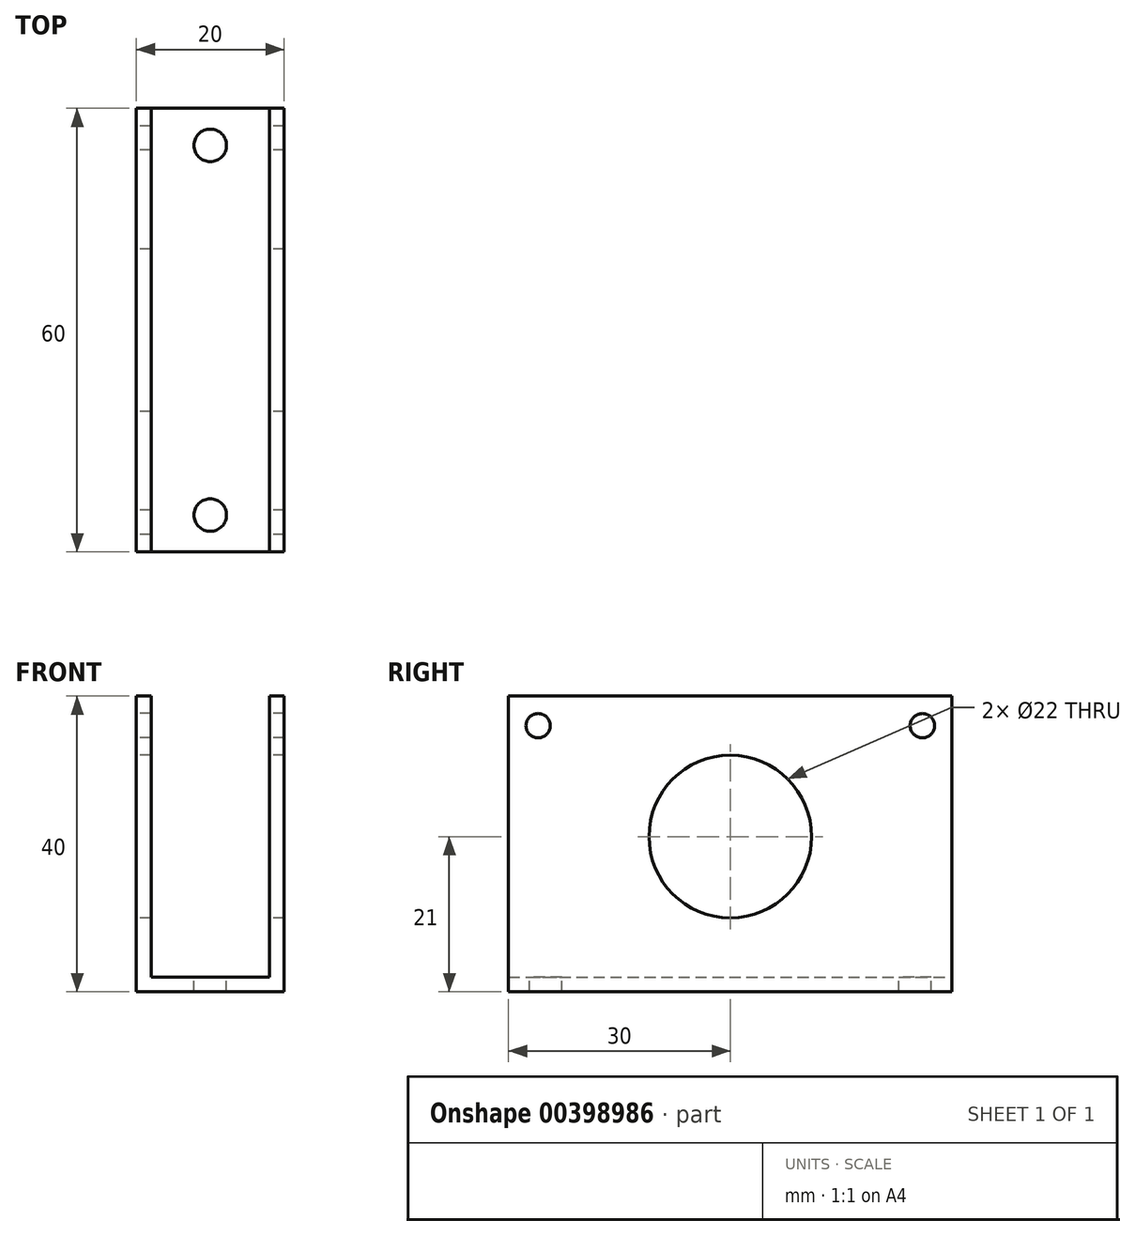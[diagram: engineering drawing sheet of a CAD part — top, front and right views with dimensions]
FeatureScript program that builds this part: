
annotation { "Feature Type Name" : "Feature", "Feature Type Description" : "" }
export const myFeature = defineFeature(function(context is Context, id is Id, definition is map)
    precondition{}
    {
        {
            var Q0;
            Q0=qCreatedBy(makeId("Front.planeOp"),FACE);
            var sketch = newSketch(context, id + "F0", { "sketchPlane" : qUnion([Q0])});
            skLineSegment(sketch, "E0", {"start": v(-10, 40) * mm, "end": v(-8, 40) * mm});
            skLineSegment(sketch, "E1", {"start": v(-8, 40) * mm, "end": v(-8, 2) * mm});
            skLineSegment(sketch, "E2", {"start": v(-8, 2) * mm, "end": v(0, 2) * mm});
            skLineSegment(sketch, "E3", {"start": v(-10, 40) * mm, "end": v(-10, 0) * mm});
            skLineSegment(sketch, "E4", {"start": v(-10, 0) * mm, "end": v(0, 0) * mm});
            skLineSegment(sketch, "E5.MirrorCS", {"start": v(8, 40) * mm, "end": v(8, 2) * mm});
            skLineSegment(sketch, "E6.MirrorCS", {"start": v(10, 40) * mm, "end": v(10, 0) * mm});
            skLineSegment(sketch, "E7.MirrorCS", {"start": v(10, 40) * mm, "end": v(8, 40) * mm});
            skLineSegment(sketch, "E8.MirrorCS", {"start": v(8, 2) * mm, "end": v(0, 2) * mm});
            skLineSegment(sketch, "E9.MirrorCS", {"start": v(10, 0) * mm, "end": v(0, 0) * mm});
            skSolve(sketch);
        }
        {
            var Q0;
            Q0=makeQuery(id+"F0.imprint","IMPRINT",FACE,{"disambiguationData":[TD([[makeQuery(id+"F0.imprint","IMPRINT",EDGE,{"derivedFrom":sQuery(id+"F0.wireOp",EDGE,"E0")}),-1.0]])]});
            extrude(context, id + "F1", {"entities" : qUnion([Q0]), "depth" : 60 * mm, "symmetric" : true});
        }
        {
            var Q0;
            Q0=makeQuery(id+"F1.opExtrude","SWEPT_FACE",FACE,{"disambiguationData":[OSD([sQuery(id+"F0.wireOp",EDGE,"E3")])]});
            var sketch = newSketch(context, id + "F2", { "sketchPlane" : qUnion([Q0])});
            skCircle(sketch, "E10", {"center": v(0, 21) * mm, "radius": 11 * mm});
            skPoint(sketch, "E11", {"position": v(-26, 36) * mm});
            skPoint(sketch, "E12.MirrorP", {"position": v(26, 36) * mm});
            skSolve(sketch);
        }
        {
            var Q0;
            Q0=makeQuery(id+"F2.imprint","IMPRINT",FACE,{"disambiguationData":[TD([[makeQuery(id+"F2.imprint","IMPRINT",EDGE,{"derivedFrom":sQuery(id+"F2.wireOp",EDGE,"E10")}),1.0]])]});
            var Q1;
            Q1=makeQuery(id+"F1.opExtrude","SWEPT_FACE",FACE,{"disambiguationData":[OSD([sQuery(id+"F0.wireOp",EDGE,"E6.MirrorCS")])]});
            extrude(context, id + "F3", {"entities" : qUnion([Q0]), "operationType" : NewBodyOperationType.REMOVE, "endBound" : BoundingType.UP_TO_SURFACE, "oppositeDirection" : true, "endBoundEntityFace" : qUnion([Q1]), "depth" : 25 * mm});
        }
        {
            var Q0;
            Q0=makeQuery(id+"F1.opExtrude","SWEPT_FACE",FACE,{"disambiguationData":[OSD([sQuery(id+"F0.wireOp",EDGE,"E2"),sQuery(id+"F0.wireOp",EDGE,"E8.MirrorCS")])]});
            var sketch = newSketch(context, id + "F4", { "sketchPlane" : qUnion([Q0])});
            skLineSegment(sketch, "E13", {"start": v(0, 30) * mm, "end": v(0, -30) * mm, "construction": true});
            skPoint(sketch, "E14", {"position": v(0, 25) * mm});
            skLineSegment(sketch, "E15", {"start": v(8, 0) * mm, "end": v(-8, 0) * mm, "construction": true});
            skPoint(sketch, "E16.MirrorP", {"position": v(0, -25) * mm});
            skSolve(sketch);
        }
        {
            var Q0;
            Q0=sQuery(id+"F4.wireOp",VERTEX,"E14");
            var Q1;
            Q1=sQuery(id+"F4.wireOp",VERTEX,"E16.MirrorP");
            var Q2;
            Q2=makeQuery(id+"F1.opExtrude","SWEPT_BODY",BODY,{"disambiguationData":[OSD([sQuery(id+"F0.wireOp",EDGE,"E0"),sQuery(id+"F0.wireOp",EDGE,"E1"),sQuery(id+"F0.wireOp",EDGE,"E2"),sQuery(id+"F0.wireOp",EDGE,"E3"),sQuery(id+"F0.wireOp",EDGE,"E4"),sQuery(id+"F0.wireOp",EDGE,"E5.MirrorCS"),sQuery(id+"F0.wireOp",EDGE,"E6.MirrorCS"),sQuery(id+"F0.wireOp",EDGE,"E7.MirrorCS"),sQuery(id+"F0.wireOp",EDGE,"E8.MirrorCS"),sQuery(id+"F0.wireOp",EDGE,"E9.MirrorCS")])]});
            hole(context, id + "F5", {"style" : HoleStyle.SIMPLE, "endStyle" : HoleEndStyle.THROUGH, "standardTappedOrClearance" : lookupTablePath({ "standard" : "ISO", "fit" : "Normal", "size" : "M4", "type" : "Clearance" }), "standardBlindInLast" : lookupTablePath({ "fit" : "Standard", "standard" : "ISO", "size" : "M4", "type" : "Clearance" }), "holeDiameter" : 4.4 * mm, "isTappedThrough" : true, "tappedDepth" : 3 * mm, "tapClearance" : 3, "locations" : qUnion([Q0, Q1]), "scope" : qUnion([Q2])});
        }
        {
            var Q0;
            Q0=sQuery(id+"F2.wireOp",VERTEX,"E11");
            var Q1;
            Q1=sQuery(id+"F2.wireOp",VERTEX,"E12.MirrorP");
            var Q2;
            Q2=makeQuery(id+"F1.opExtrude","SWEPT_BODY",BODY,{"disambiguationData":[OSD([sQuery(id+"F0.wireOp",EDGE,"E0"),sQuery(id+"F0.wireOp",EDGE,"E1"),sQuery(id+"F0.wireOp",EDGE,"E2"),sQuery(id+"F0.wireOp",EDGE,"E3"),sQuery(id+"F0.wireOp",EDGE,"E4"),sQuery(id+"F0.wireOp",EDGE,"E5.MirrorCS"),sQuery(id+"F0.wireOp",EDGE,"E6.MirrorCS"),sQuery(id+"F0.wireOp",EDGE,"E7.MirrorCS"),sQuery(id+"F0.wireOp",EDGE,"E8.MirrorCS"),sQuery(id+"F0.wireOp",EDGE,"E9.MirrorCS")])]});
            hole(context, id + "F6", {"style" : HoleStyle.SIMPLE, "endStyle" : HoleEndStyle.THROUGH, "standardTappedOrClearance" : lookupTablePath({ "standard" : "ISO", "fit" : "Normal", "size" : "M3", "type" : "Clearance" }), "standardBlindInLast" : lookupTablePath({ "fit" : "Standard", "standard" : "ISO", "size" : "M3", "type" : "Clearance" }), "holeDiameter" : 3.3 * mm, "isTappedThrough" : true, "tappedDepth" : 3 * mm, "tapClearance" : 3, "locations" : qUnion([Q0, Q1]), "scope" : qUnion([Q2])});
        }
    });
